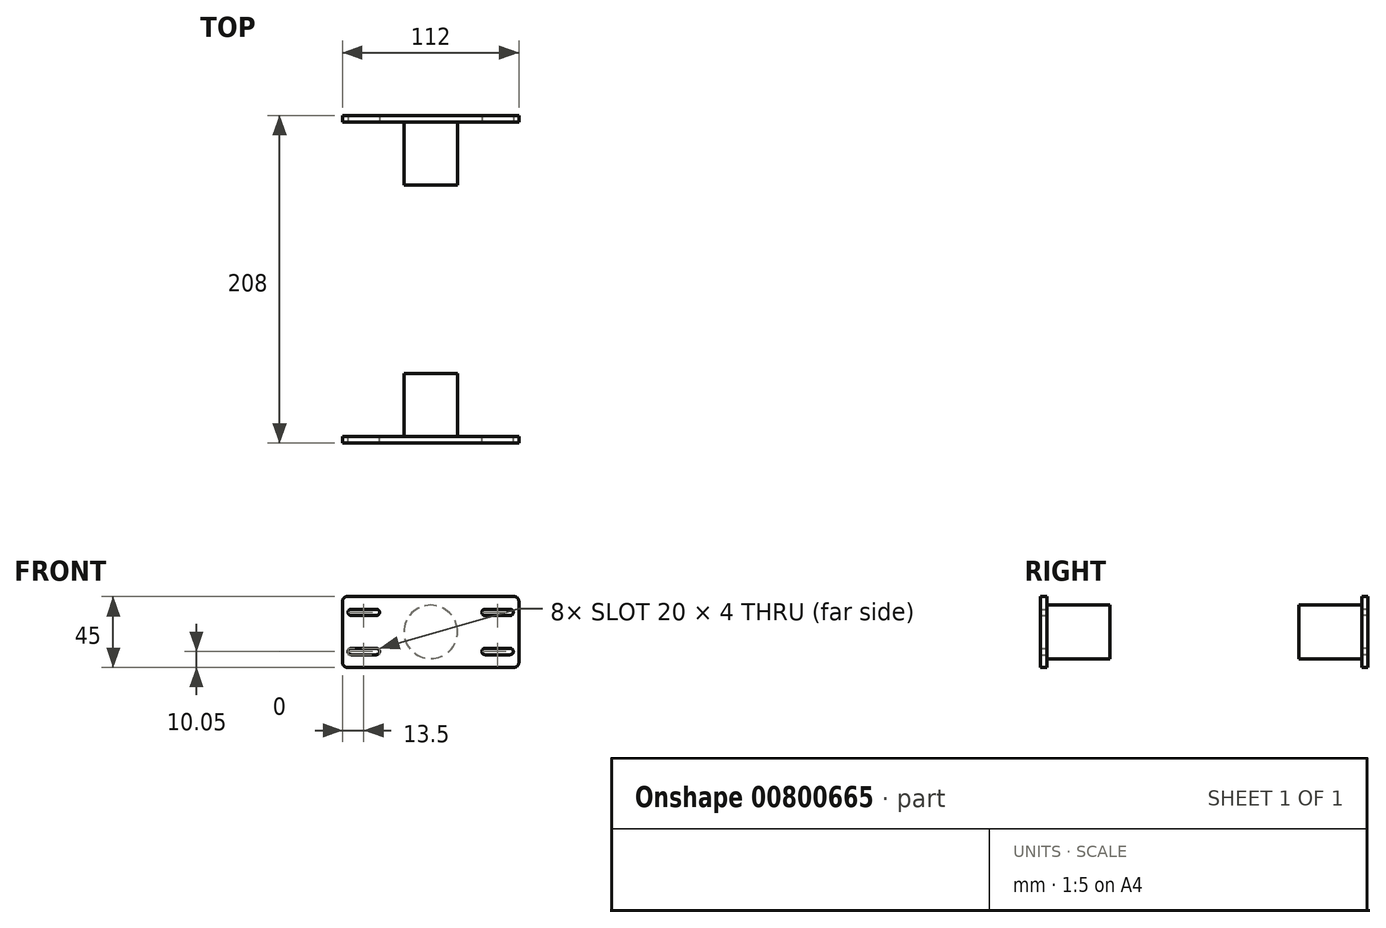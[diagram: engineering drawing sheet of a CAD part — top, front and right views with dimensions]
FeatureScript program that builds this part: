
annotation { "Feature Type Name" : "Feature", "Feature Type Description" : "" }
export const myFeature = defineFeature(function(context is Context, id is Id, definition is map)
    precondition{}
    {
        {
            var Q0;
            Q0=qCreatedBy(makeId("Front.planeOp"),FACE);
            var sketch = newSketch(context, id + "F0", { "sketchPlane" : qUnion([Q0])});
            skLineSegment(sketch, "E0.bottom", {"start": v(53, 22.5) * mm, "end": v(-53, 22.5) * mm});
            skLineSegment(sketch, "E0.top", {"start": v(53, -22.5) * mm, "end": v(-53, -22.5) * mm});
            skLineSegment(sketch, "E0.left", {"start": v(56, 19.5) * mm, "end": v(56, -19.5) * mm});
            skLineSegment(sketch, "E0.right", {"start": v(-56, 19.5) * mm, "end": v(-56, -19.5) * mm});
            skPoint(sketch, "E0.middle", {"position": v(0, 0) * mm});
            skLineSegment(sketch, "E1", {"start": v(0, 0) * mm, "end": v(0, 27.78) * mm, "construction": true});
            skLineSegment(sketch, "E2", {"start": v(0, 0) * mm, "end": v(41.9, 0) * mm, "construction": true});
            skLineSegment(sketch, "E3.bottom", {"start": v(34.5, 14.45) * mm, "end": v(50.5, 14.45) * mm});
            skLineSegment(sketch, "E3.top", {"start": v(34.5, 10.45) * mm, "end": v(50.5, 10.45) * mm});
            skLineSegment(sketch, "E3.left", {"start": v(32.5, 12.45) * mm, "end": v(32.5, 12.45) * mm});
            skLineSegment(sketch, "E3.right", {"start": v(52.5, 12.45) * mm, "end": v(52.5, 12.45) * mm});
            skPoint(sketch, "E4.visualSharp", {"position": v(32.5, 14.45) * mm});
            skArc(sketch, "E4.filletArc", {"start": v(34.5, 14.45) * mm, "mid": v(33.09, 13.86) * mm, "end": v(32.5, 12.45) * mm});
            skPoint(sketch, "E5.visualSharp", {"position": v(32.5, 10.45) * mm});
            skArc(sketch, "E5.filletArc", {"start": v(32.5, 12.45) * mm, "mid": v(33.09, 11.04) * mm, "end": v(34.5, 10.45) * mm});
            skPoint(sketch, "E6.visualSharp", {"position": v(52.5, 10.45) * mm});
            skArc(sketch, "E6.filletArc", {"start": v(50.5, 10.45) * mm, "mid": v(51.91, 11.04) * mm, "end": v(52.5, 12.45) * mm});
            skPoint(sketch, "E7.visualSharp", {"position": v(52.5, 14.45) * mm});
            skArc(sketch, "E7.filletArc", {"start": v(52.5, 12.45) * mm, "mid": v(51.91, 13.86) * mm, "end": v(50.5, 14.45) * mm});
            skLineSegment(sketch, "E8.MirrorCS", {"start": v(34.5, -10.45) * mm, "end": v(50.5, -10.45) * mm});
            skArc(sketch, "E9.MirrorCS", {"start": v(50.5, -10.45) * mm, "mid": v(51.91, -11.04) * mm, "end": v(52.5, -12.45) * mm});
            skLineSegment(sketch, "E10.MirrorCS", {"start": v(52.5, -12.45) * mm, "end": v(52.5, -12.45) * mm});
            skArc(sketch, "E11.MirrorCS", {"start": v(52.5, -12.45) * mm, "mid": v(51.91, -13.86) * mm, "end": v(50.5, -14.45) * mm});
            skLineSegment(sketch, "E12.MirrorCS", {"start": v(34.5, -14.45) * mm, "end": v(50.5, -14.45) * mm});
            skArc(sketch, "E13.MirrorCS", {"start": v(34.5, -14.45) * mm, "mid": v(33.09, -13.86) * mm, "end": v(32.5, -12.45) * mm});
            skLineSegment(sketch, "E14.MirrorCS", {"start": v(32.5, -12.45) * mm, "end": v(32.5, -12.45) * mm});
            skArc(sketch, "E15.MirrorCS", {"start": v(32.5, -12.45) * mm, "mid": v(33.09, -11.04) * mm, "end": v(34.5, -10.45) * mm});
            skLineSegment(sketch, "E16.MirrorCS", {"start": v(-52.5, 12.45) * mm, "end": v(-52.5, 12.45) * mm});
            skArc(sketch, "E17.MirrorCS", {"start": v(-32.5, -12.45) * mm, "mid": v(-33.09, -11.04) * mm, "end": v(-34.5, -10.45) * mm});
            skArc(sketch, "E18.MirrorCS", {"start": v(-34.5, -14.45) * mm, "mid": v(-33.09, -13.86) * mm, "end": v(-32.5, -12.45) * mm});
            skLineSegment(sketch, "E19.MirrorCS", {"start": v(-32.5, -12.45) * mm, "end": v(-32.5, -12.45) * mm});
            skLineSegment(sketch, "E20.MirrorCS", {"start": v(-52.5, -12.45) * mm, "end": v(-52.5, -12.45) * mm});
            skLineSegment(sketch, "E21.MirrorCS", {"start": v(-32.5, 12.45) * mm, "end": v(-32.5, 12.45) * mm});
            skArc(sketch, "E22.MirrorCS", {"start": v(-50.5, 10.45) * mm, "mid": v(-51.91, 11.04) * mm, "end": v(-52.5, 12.45) * mm});
            skArc(sketch, "E23.MirrorCS", {"start": v(-52.5, 12.45) * mm, "mid": v(-51.91, 13.86) * mm, "end": v(-50.5, 14.45) * mm});
            skArc(sketch, "E24.MirrorCS", {"start": v(-34.5, 14.45) * mm, "mid": v(-33.09, 13.86) * mm, "end": v(-32.5, 12.45) * mm});
            skArc(sketch, "E25.MirrorCS", {"start": v(-32.5, 12.45) * mm, "mid": v(-33.09, 11.04) * mm, "end": v(-34.5, 10.45) * mm});
            skPoint(sketch, "E26.MirrorP", {"position": v(-32.5, 10.45) * mm});
            skLineSegment(sketch, "E27.MirrorCS", {"start": v(-34.5, 10.45) * mm, "end": v(-50.5, 10.45) * mm});
            skArc(sketch, "E28.MirrorCS", {"start": v(-50.5, -10.45) * mm, "mid": v(-51.91, -11.04) * mm, "end": v(-52.5, -12.45) * mm});
            skPoint(sketch, "E29.MirrorP", {"position": v(-32.5, 14.45) * mm});
            skLineSegment(sketch, "E30.MirrorCS", {"start": v(-34.5, -14.45) * mm, "end": v(-50.5, -14.45) * mm});
            skLineSegment(sketch, "E31.MirrorCS", {"start": v(-34.5, 14.45) * mm, "end": v(-50.5, 14.45) * mm});
            skPoint(sketch, "E32.MirrorP", {"position": v(-52.5, 14.45) * mm});
            skArc(sketch, "E33.MirrorCS", {"start": v(-52.5, -12.45) * mm, "mid": v(-51.91, -13.86) * mm, "end": v(-50.5, -14.45) * mm});
            skLineSegment(sketch, "E34.MirrorCS", {"start": v(-34.5, -10.45) * mm, "end": v(-50.5, -10.45) * mm});
            skPoint(sketch, "E35.MirrorP", {"position": v(-52.5, 10.45) * mm});
            skPoint(sketch, "E36.visualSharp", {"position": v(-56, 22.5) * mm});
            skArc(sketch, "E36.filletArc", {"start": v(-53, 22.5) * mm, "mid": v(-55.12, 21.62) * mm, "end": v(-56, 19.5) * mm});
            skPoint(sketch, "E37.visualSharp", {"position": v(-56, -22.5) * mm});
            skArc(sketch, "E37.filletArc", {"start": v(-56, -19.5) * mm, "mid": v(-55.12, -21.62) * mm, "end": v(-53, -22.5) * mm});
            skPoint(sketch, "E38.visualSharp", {"position": v(56, -22.5) * mm});
            skArc(sketch, "E38.filletArc", {"start": v(53, -22.5) * mm, "mid": v(55.12, -21.62) * mm, "end": v(56, -19.5) * mm});
            skPoint(sketch, "E39.visualSharp", {"position": v(56, 22.5) * mm});
            skArc(sketch, "E39.filletArc", {"start": v(56, 19.5) * mm, "mid": v(55.12, 21.62) * mm, "end": v(53, 22.5) * mm});
            skSolve(sketch);
        }
        {
            var Q0;
            Q0 = qSketchRegion(id + "F0", true);
            extrude(context, id + "F1", {"entities" : qUnion([Q0]), "depth" : 4 * mm, "offsetDistance" : 25 * mm});
        }
        {
            var Q0;
            Q0=makeQuery(id+"F1.opExtrude","CAP_FACE",FACE,{"disambiguationData":[OSD([sQuery(id+"F0.wireOp",EDGE,"E0.bottom"),sQuery(id+"F0.wireOp",EDGE,"E0.top"),sQuery(id+"F0.wireOp",EDGE,"E0.left"),sQuery(id+"F0.wireOp",EDGE,"E0.right"),sQuery(id+"F0.wireOp",EDGE,"E3.bottom"),sQuery(id+"F0.wireOp",EDGE,"E3.top"),sQuery(id+"F0.wireOp",EDGE,"E4.filletArc"),sQuery(id+"F0.wireOp",EDGE,"E5.filletArc"),sQuery(id+"F0.wireOp",EDGE,"E6.filletArc"),sQuery(id+"F0.wireOp",EDGE,"E7.filletArc"),sQuery(id+"F0.wireOp",EDGE,"E8.MirrorCS"),sQuery(id+"F0.wireOp",EDGE,"E9.MirrorCS"),sQuery(id+"F0.wireOp",EDGE,"E11.MirrorCS"),sQuery(id+"F0.wireOp",EDGE,"E12.MirrorCS"),sQuery(id+"F0.wireOp",EDGE,"E13.MirrorCS"),sQuery(id+"F0.wireOp",EDGE,"E15.MirrorCS"),sQuery(id+"F0.wireOp",EDGE,"E17.MirrorCS"),sQuery(id+"F0.wireOp",EDGE,"E18.MirrorCS"),sQuery(id+"F0.wireOp",EDGE,"E22.MirrorCS"),sQuery(id+"F0.wireOp",EDGE,"E23.MirrorCS"),sQuery(id+"F0.wireOp",EDGE,"E24.MirrorCS"),sQuery(id+"F0.wireOp",EDGE,"E25.MirrorCS"),sQuery(id+"F0.wireOp",EDGE,"E27.MirrorCS"),sQuery(id+"F0.wireOp",EDGE,"E28.MirrorCS"),sQuery(id+"F0.wireOp",EDGE,"E30.MirrorCS"),sQuery(id+"F0.wireOp",EDGE,"E31.MirrorCS"),sQuery(id+"F0.wireOp",EDGE,"E33.MirrorCS"),sQuery(id+"F0.wireOp",EDGE,"E34.MirrorCS"),sQuery(id+"F0.wireOp",EDGE,"E36.filletArc"),sQuery(id+"F0.wireOp",EDGE,"E37.filletArc"),sQuery(id+"F0.wireOp",EDGE,"E38.filletArc"),sQuery(id+"F0.wireOp",EDGE,"E39.filletArc")])],"isStart":true});
            var sketch = newSketch(context, id + "F2", { "sketchPlane" : qUnion([Q0])});
            skCircle(sketch, "E40", {"center": v(0, 0) * mm, "radius": 17 * mm});
            skSolve(sketch);
        }
        {
            var Q0;
            Q0 = qSketchRegion(id + "F2", true);
            extrude(context, id + "F3", {"entities" : qUnion([Q0]), "operationType" : NewBodyOperationType.ADD, "depth" : 40 * mm, "offsetDistance" : 25 * mm});
        }
        {
            var Q0;
            Q0=makeQuery(id+"F1.opExtrude","CAP_FACE",FACE,{"disambiguationData":[OSD([sQuery(id+"F0.wireOp",EDGE,"E0.bottom"),sQuery(id+"F0.wireOp",EDGE,"E0.top"),sQuery(id+"F0.wireOp",EDGE,"E0.left"),sQuery(id+"F0.wireOp",EDGE,"E0.right"),sQuery(id+"F0.wireOp",EDGE,"E3.bottom"),sQuery(id+"F0.wireOp",EDGE,"E3.top"),sQuery(id+"F0.wireOp",EDGE,"E4.filletArc"),sQuery(id+"F0.wireOp",EDGE,"E5.filletArc"),sQuery(id+"F0.wireOp",EDGE,"E6.filletArc"),sQuery(id+"F0.wireOp",EDGE,"E7.filletArc"),sQuery(id+"F0.wireOp",EDGE,"E8.MirrorCS"),sQuery(id+"F0.wireOp",EDGE,"E9.MirrorCS"),sQuery(id+"F0.wireOp",EDGE,"E11.MirrorCS"),sQuery(id+"F0.wireOp",EDGE,"E12.MirrorCS"),sQuery(id+"F0.wireOp",EDGE,"E13.MirrorCS"),sQuery(id+"F0.wireOp",EDGE,"E15.MirrorCS"),sQuery(id+"F0.wireOp",EDGE,"E17.MirrorCS"),sQuery(id+"F0.wireOp",EDGE,"E18.MirrorCS"),sQuery(id+"F0.wireOp",EDGE,"E22.MirrorCS"),sQuery(id+"F0.wireOp",EDGE,"E23.MirrorCS"),sQuery(id+"F0.wireOp",EDGE,"E24.MirrorCS"),sQuery(id+"F0.wireOp",EDGE,"E25.MirrorCS"),sQuery(id+"F0.wireOp",EDGE,"E27.MirrorCS"),sQuery(id+"F0.wireOp",EDGE,"E28.MirrorCS"),sQuery(id+"F0.wireOp",EDGE,"E30.MirrorCS"),sQuery(id+"F0.wireOp",EDGE,"E31.MirrorCS"),sQuery(id+"F0.wireOp",EDGE,"E33.MirrorCS"),sQuery(id+"F0.wireOp",EDGE,"E34.MirrorCS"),sQuery(id+"F0.wireOp",EDGE,"E36.filletArc"),sQuery(id+"F0.wireOp",EDGE,"E37.filletArc"),sQuery(id+"F0.wireOp",EDGE,"E38.filletArc"),sQuery(id+"F0.wireOp",EDGE,"E39.filletArc")])],"isStart":true});
            cPlane(context, id + "F4", {"entities" : qUnion([Q0]), "cplaneType" : CPlaneType.OFFSET, "offset" : 100 * mm, "width" : 150 * mm, "height" : 150 * mm});
        }
        {
            var Q0;
            Q0=makeQuery(id+"F1.opExtrude","SWEPT_BODY",BODY,{"disambiguationData":[OSD([sQuery(id+"F0.wireOp",EDGE,"E0.bottom"),sQuery(id+"F0.wireOp",EDGE,"E0.top"),sQuery(id+"F0.wireOp",EDGE,"E0.left"),sQuery(id+"F0.wireOp",EDGE,"E0.right"),sQuery(id+"F0.wireOp",EDGE,"E3.bottom"),sQuery(id+"F0.wireOp",EDGE,"E3.top"),sQuery(id+"F0.wireOp",EDGE,"E4.filletArc"),sQuery(id+"F0.wireOp",EDGE,"E5.filletArc"),sQuery(id+"F0.wireOp",EDGE,"E6.filletArc"),sQuery(id+"F0.wireOp",EDGE,"E7.filletArc"),sQuery(id+"F0.wireOp",EDGE,"E8.MirrorCS"),sQuery(id+"F0.wireOp",EDGE,"E9.MirrorCS"),sQuery(id+"F0.wireOp",EDGE,"E11.MirrorCS"),sQuery(id+"F0.wireOp",EDGE,"E12.MirrorCS"),sQuery(id+"F0.wireOp",EDGE,"E13.MirrorCS"),sQuery(id+"F0.wireOp",EDGE,"E15.MirrorCS"),sQuery(id+"F0.wireOp",EDGE,"E17.MirrorCS"),sQuery(id+"F0.wireOp",EDGE,"E18.MirrorCS"),sQuery(id+"F0.wireOp",EDGE,"E22.MirrorCS"),sQuery(id+"F0.wireOp",EDGE,"E23.MirrorCS"),sQuery(id+"F0.wireOp",EDGE,"E24.MirrorCS"),sQuery(id+"F0.wireOp",EDGE,"E25.MirrorCS"),sQuery(id+"F0.wireOp",EDGE,"E27.MirrorCS"),sQuery(id+"F0.wireOp",EDGE,"E28.MirrorCS"),sQuery(id+"F0.wireOp",EDGE,"E30.MirrorCS"),sQuery(id+"F0.wireOp",EDGE,"E31.MirrorCS"),sQuery(id+"F0.wireOp",EDGE,"E33.MirrorCS"),sQuery(id+"F0.wireOp",EDGE,"E34.MirrorCS"),sQuery(id+"F0.wireOp",EDGE,"E36.filletArc"),sQuery(id+"F0.wireOp",EDGE,"E37.filletArc"),sQuery(id+"F0.wireOp",EDGE,"E38.filletArc"),sQuery(id+"F0.wireOp",EDGE,"E39.filletArc")])]});
            var Q1;
            Q1=qCreatedBy(id+"F4.planeOp",FACE);
            mirror(context, id + "F5", {"entities" : qUnion([Q0]), "mirrorPlane" : qUnion([Q1])});
        }
    });
